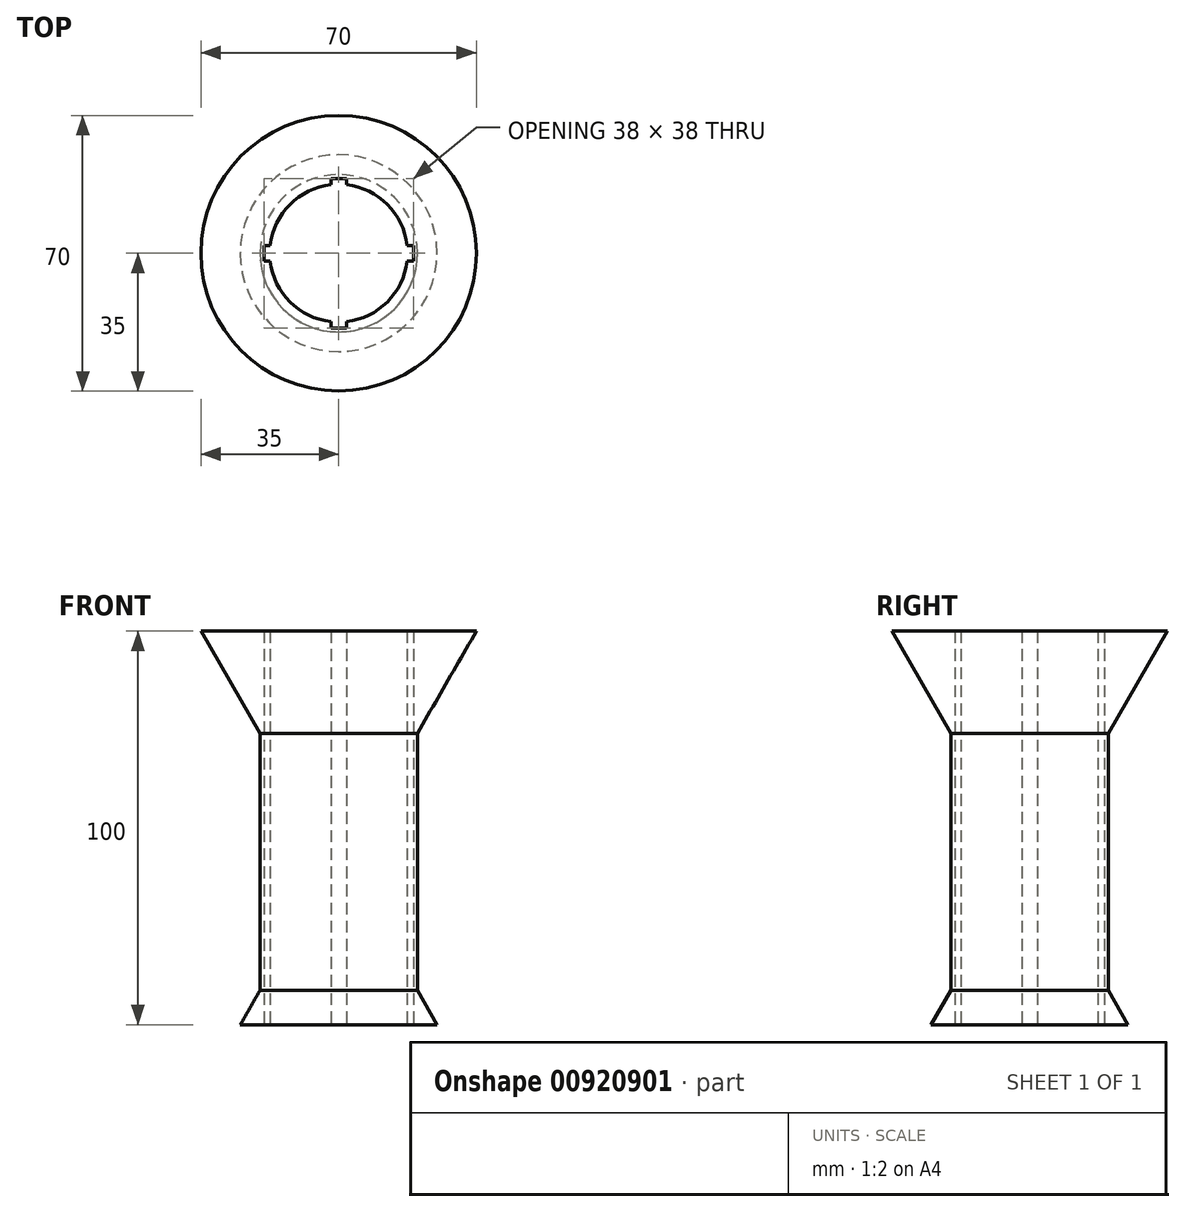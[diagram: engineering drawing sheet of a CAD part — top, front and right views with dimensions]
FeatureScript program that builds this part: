
annotation { "Feature Type Name" : "Feature", "Feature Type Description" : "" }
export const myFeature = defineFeature(function(context is Context, id is Id, definition is map)
    precondition{}
    {
        {
            var Q0;
            Q0=qCreatedBy(makeId("Top.planeOp"),FACE);
            var sketch = newSketch(context, id + "F0", { "sketchPlane" : qUnion([Q0])});
            skCircle(sketch, "E0", {"center": v(0, 0) * mm, "radius": 20 * mm});
            skArc(sketch, "E1", {"start": v(17.39, 2) * mm, "mid": v(12.37, 12.37) * mm, "end": v(2, 17.39) * mm});
            skLineSegment(sketch, "E2.bottom", {"start": v(-19, 2) * mm, "end": v(-17.39, 2) * mm});
            skLineSegment(sketch, "E2.top", {"start": v(-19, -2) * mm, "end": v(-17.39, -2) * mm});
            skLineSegment(sketch, "E2.left", {"start": v(-19, 2) * mm, "end": v(-19, -2) * mm});
            skLineSegment(sketch, "E2.right", {"start": v(19, 2) * mm, "end": v(19, -2) * mm});
            skLineSegment(sketch, "E3", {"start": v(-27.64, 0) * mm, "end": v(39.71, 0) * mm, "construction": true});
            skLineSegment(sketch, "E4", {"start": v(0, -24.7) * mm, "end": v(0, 27.29) * mm, "construction": true});
            skArc(sketch, "E5.trimOffspring", {"start": v(-17.39, -2) * mm, "mid": v(-12.37, -12.37) * mm, "end": v(-2, -17.39) * mm});
            skLineSegment(sketch, "E6.trimOffspring", {"start": v(17.39, 2) * mm, "end": v(19, 2) * mm});
            skLineSegment(sketch, "E7.trimOffspring", {"start": v(17.39, -2) * mm, "end": v(19, -2) * mm});
            skLineSegment(sketch, "E8", {"start": v(-18.8, -18.8) * mm, "end": v(0, 0) * mm, "construction": true});
            skLineSegment(sketch, "E9", {"start": v(0, 0) * mm, "end": v(14.73, -14.73) * mm, "construction": true});
            skLineSegment(sketch, "E10.MirrorCS", {"start": v(2, -19) * mm, "end": v(2, -17.39) * mm});
            skLineSegment(sketch, "E11.MirrorCS", {"start": v(2, -19) * mm, "end": v(-2, -19) * mm});
            skLineSegment(sketch, "E12.MirrorCS", {"start": v(-2, -19) * mm, "end": v(-2, -17.39) * mm});
            skLineSegment(sketch, "E13.MirrorCS", {"start": v(-2, 17.39) * mm, "end": v(-2, 19) * mm});
            skLineSegment(sketch, "E14.MirrorCS", {"start": v(2, 17.39) * mm, "end": v(2, 19) * mm});
            skLineSegment(sketch, "E15.MirrorCS", {"start": v(2, 19) * mm, "end": v(-2, 19) * mm});
            skArc(sketch, "E16.trimOffspring", {"start": v(-2, 17.39) * mm, "mid": v(-12.37, 12.37) * mm, "end": v(-17.39, 2) * mm});
            skArc(sketch, "E17.trimOffspring", {"start": v(2, -17.39) * mm, "mid": v(12.37, -12.37) * mm, "end": v(17.39, -2) * mm});
            skSolve(sketch);
        }
        {
            var Q0;
            Q0 = qSketchRegion(id + "F0", true);
            extrude(context, id + "F1", {"entities" : qUnion([Q0]), "depth" : 100 * mm, "offsetDistance" : 25 * mm});
        }
        {
            var Q0;
            Q0=qCreatedBy(makeId("Front.planeOp"),FACE);
            var sketch = newSketch(context, id + "F2", { "sketchPlane" : qUnion([Q0])});
            skLineSegment(sketch, "E18", {"start": v(20, 100) * mm, "end": v(20, 74.02) * mm});
            skLineSegment(sketch, "E19", {"start": v(20, 74.02) * mm, "end": v(35, 100) * mm});
            skLineSegment(sketch, "E20", {"start": v(35, 100) * mm, "end": v(20, 100) * mm});
            skLineSegment(sketch, "E21", {"start": v(0, 0) * mm, "end": v(0, 110.34) * mm, "construction": true});
            skLineSegment(sketch, "E22", {"start": v(20, 8.66) * mm, "end": v(20, 0) * mm});
            skLineSegment(sketch, "E23", {"start": v(20, 0) * mm, "end": v(25, 0) * mm});
            skLineSegment(sketch, "E24", {"start": v(25, 0) * mm, "end": v(20, 8.66) * mm});
            skSolve(sketch);
        }
        {
            var Q0;
            Q0=qCreatedBy(makeId("Front.planeOp"),FACE);
            var sketch = newSketch(context, id + "F3", { "sketchPlane" : qUnion([Q0])});
            skLineSegment(sketch, "E25", {"start": v(0, 120.6) * mm, "end": v(0, 0) * mm});
            skSolve(sketch);
        }
        {
            var Q0;
            Q0=makeQuery(id+"F2.imprint","IMPRINT",FACE,{"disambiguationData":[TD([[makeQuery(id+"F2.imprint","IMPRINT",EDGE,{"derivedFrom":sQuery(id+"F2.wireOp",EDGE,"E18")}),1.0]])]});
            var Q1;
            Q1=makeQuery(id+"F2.imprint","IMPRINT",FACE,{"disambiguationData":[TD([[makeQuery(id+"F2.imprint","IMPRINT",EDGE,{"derivedFrom":sQuery(id+"F2.wireOp",EDGE,"E22")}),1.0]])]});
            var Q2;
            Q2=sQuery(id+"F3.wireOp",EDGE,"E25");
            revolve(context, id + "F4", {"operationType" : NewBodyOperationType.ADD, "surfaceOperationType" : NewSurfaceOperationType.NEW, "entities" : qUnion([Q0, Q1]), "axis" : qUnion([Q2]), "revolveType" : RevolveType.FULL});
        }
    });
